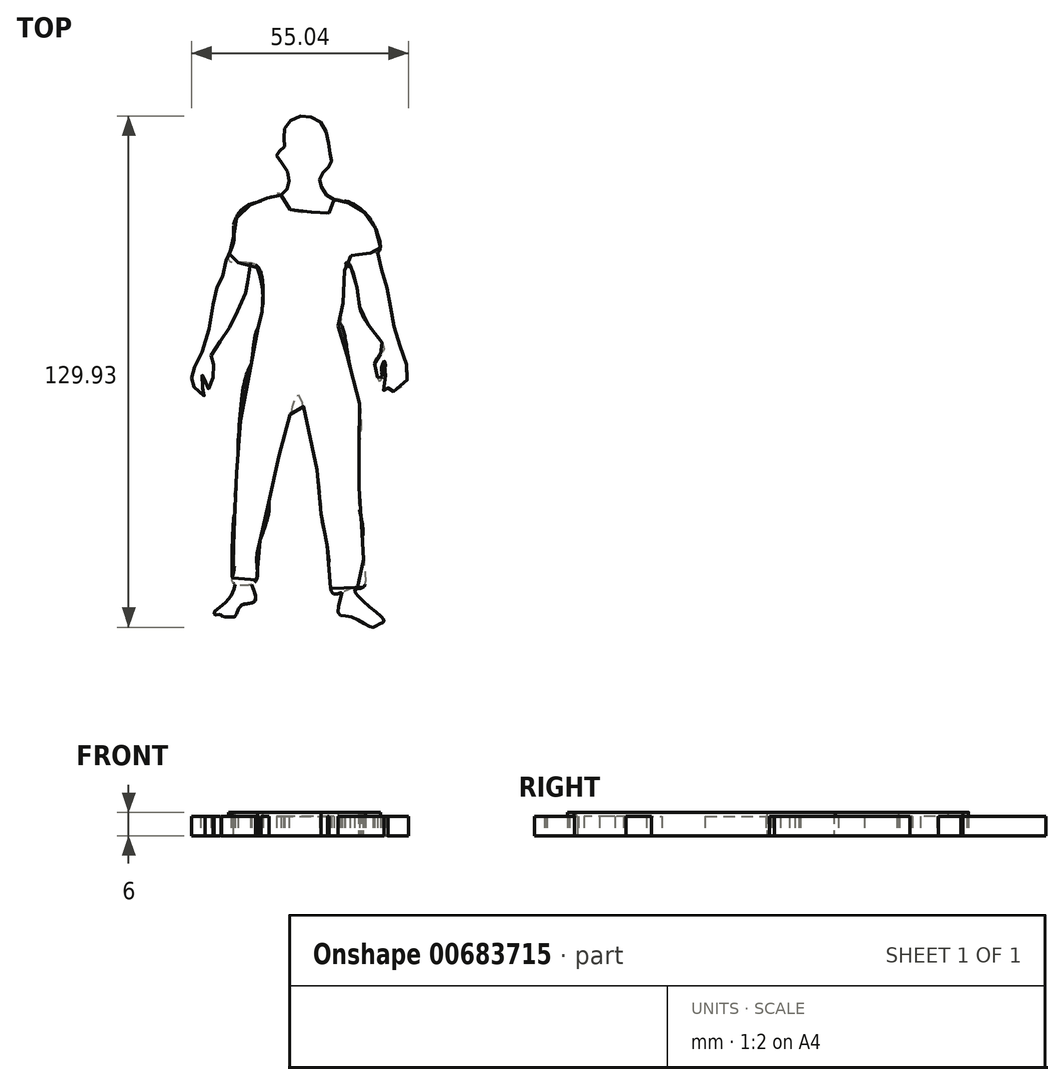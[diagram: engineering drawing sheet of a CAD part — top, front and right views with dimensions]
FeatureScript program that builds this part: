
annotation { "Feature Type Name" : "Feature", "Feature Type Description" : "" }
export const myFeature = defineFeature(function(context is Context, id is Id, definition is map)
    precondition{}
    {
        {
            var Q0;
            Q0=qCreatedBy(makeId("Top.planeOp"),FACE);
            var sketch = newSketch(context, id + "F0", { "sketchPlane" : qUnion([Q0])});
            skFitSpline(sketch, "E0", {"points": [v(-30.35, 51.78) * mm, v(-29.82, 47) * mm, v(-33, 44.36) * mm, v(-40.42, 42.24) * mm, v(-43.6, 37.47) * mm, v(-43.6, 33.23) * mm, v(-44.13, 31.38) * mm, v(-45.45, 29) * mm, v(-46.5, 23.96) * mm, v(-47.83, 21.58) * mm, v(-49.42, 13.37) * mm, v(-52.6, 3.03) * mm, v(-54.2, 0) * mm, v(-54.2, -2.26) * mm, v(-53.66, -3.85) * mm, v(-51.01, -5.97) * mm, v(-51.01, -4.91) * mm, v(-52.07, -2.26) * mm, v(-51.01, 0) * mm, v(-51.01, -3.85) * mm, v(-49.42, -3.85) * mm, v(-48.9, 0) * mm, v(-48.9, 2.5) * mm, v(-49.42, 4.1) * mm, v(-46.24, 8.86) * mm, v(-43.6, 13.63) * mm, v(-40.42, 20.52) * mm, v(-40.15, 22.1) * mm, v(-39.1, 28.2) * mm, v(-37.24, 25.29) * mm, v(-36.18, 18.93) * mm, v(-36.97, 11.51) * mm, v(-38.03, 9.13) * mm, v(-38.03, 5.68) * mm, v(-40.15, 0) * mm, v(-41.48, -5.97) * mm, v(-42.54, -19.22) * mm, v(-42.54, -25.05) * mm, v(-43.6, -36.44) * mm, v(-43.6, -53.66) * mm, v(-43.33, -53.66) * mm, v(-44.65, -57.37) * mm, v(-48.63, -61.07) * mm, v(-48.36, -61.6) * mm, v(-47.57, -61.6) * mm, v(-46.77, -61.6) * mm, v(-46.77, -61.87) * mm, v(-45.45, -62.13) * mm, v(-44.13, -62.13) * mm, v(-43.33, -62.13) * mm, v(-42, -59.49) * mm, v(-39.36, -58.7) * mm, v(-38.03, -57.37) * mm, v(-39.1, -53.66) * mm, v(-38.83, -53.66) * mm, v(-38.3, -47.83) * mm, v(-34.85, -36.44) * mm, v(-34.59, -29.82) * mm, v(-31.94, -18.69) * mm, v(-27.17, -4.91) * mm, v(-22.93, -20.28) * mm, v(-20.28, -31.93) * mm, v(-20.28, -37.23) * mm, v(-17.1, -55.78) * mm, v(-16.04, -55.51) * mm, v(-17.1, -61.07) * mm, v(-13.93, -62.13) * mm, v(-8.63, -64.78) * mm, v(-7.04, -64.25) * mm, v(-5.45, -63.2) * mm, v(-8.63, -60.02) * mm, v(-12.87, -55.25) * mm, v(-10.75, -54.72) * mm, v(-11.28, -52.07) * mm, v(-10.75, -41.47) * mm, v(-11.8, -34.58) * mm, v(-12.87, -26.64) * mm, v(-11.8, -17.1) * mm, v(-11.8, -10.74) * mm, v(-14.46, 3.56) * mm, v(-16.04, 11.51) * mm, v(-16.84, 13.1) * mm, v(-16.04, 23.96) * mm, v(-14.72, 27.94) * mm, v(-12.34, 21.58) * mm, v(-10.48, 13.63) * mm, v(-5.45, 5.95) * mm, v(-7.57, 3.56) * mm, v(-7.3, 0) * mm, v(-6.5, -2.26) * mm, v(-5.45, 0) * mm, v(-5.98, 0) * mm, v(-5.45, 2.77) * mm, v(-5.18, -2.26) * mm, v(-5.45, -4.65) * mm, v(-4.39, -3.85) * mm, v(-4.39, -4.91) * mm, v(0, -2.8) * mm, v(0, 2.77) * mm, v(-2.8, 11.51) * mm, v(-4.39, 19.99) * mm, v(-6.5, 27.94) * mm, v(-7.57, 34.3) * mm, v(-8.63, 38.53) * mm, v(-14.46, 43.3) * mm, v(-18.16, 43.83) * mm, v(-21.34, 47) * mm, v(-21.34, 50.19) * mm, v(-18.96, 52.84) * mm, v(-19.22, 56.02) * mm, v(-21.08, 62.9) * mm, v(-26.64, 65.02) * mm, v(-30.88, 61.31) * mm, v(-30.88, 57.08) * mm, v(-32.73, 55.49) * mm, v(-30.35, 51.78) * mm]});
            skSolve(sketch);
        }
        {
            var Q0;
            Q0=qCreatedBy(makeId("Top.planeOp"),FACE);
            var sketch = newSketch(context, id + "F1", { "sketchPlane" : qUnion([Q0])});
            skFitSpline(sketch, "E1", {"points": [v(-37.24, 11.51) * mm, v(-31.67, 11.51) * mm, v(-16.57, 11.51) * mm, v(-15.78, 9.13) * mm, v(-13.66, 0) * mm, v(-11.28, -11.27) * mm, v(-11.8, -20.28) * mm, v(-11.8, -27.96) * mm, v(-11.8, -34.05) * mm, v(-10.75, -41.47) * mm, v(-10.75, -46.24) * mm, v(-10.48, -54.45) * mm, v(-12.87, -54.72) * mm, v(-18.16, -56.3) * mm, v(-19.22, -51) * mm, v(-20.28, -42) * mm, v(-21.34, -37.76) * mm, v(-21.34, -32.46) * mm, v(-24, -17.1) * mm, v(-27.44, -5.7) * mm, v(-29.82, -13.4) * mm, v(-31.94, -20.8) * mm, v(-34.59, -32.2) * mm, v(-35.65, -38.82) * mm, v(-37.77, -47.3) * mm, v(-38.3, -53.4) * mm, v(-43.6, -53.66) * mm, v(-43.6, -50.48) * mm, v(-43.6, -37.23) * mm, v(-42.54, -21.34) * mm, v(-41.48, -8.89) * mm, v(-39.1, 2.5) * mm, v(-37.24, 11.51) * mm]});
            skSolve(sketch);
        }
        {
            var Q0;
            Q0=qCreatedBy(makeId("Top.planeOp"),FACE);
            var sketch = newSketch(context, id + "F2", { "sketchPlane" : qUnion([Q0])});
            skFitSpline(sketch, "E2", {"points": [v(-31.94, 45.42) * mm, v(-29.82, 41.71) * mm, v(-23.46, 40.65) * mm, v(-19.22, 40.65) * mm, v(-18.16, 43.83) * mm, v(-14.98, 43.3) * mm, v(-10.75, 40.92) * mm, v(-7.3, 35.88) * mm, v(-6.5, 31.11) * mm, v(-8.36, 30.32) * mm, v(-13.93, 29.52) * mm, v(-15.51, 25.29) * mm, v(-16.84, 12.04) * mm, v(-18.7, 11.51) * mm, v(-28.76, 11.25) * mm, v(-37.24, 10.98) * mm, v(-36.7, 14.16) * mm, v(-36.18, 19.99) * mm, v(-38.3, 27.4) * mm, v(-44.65, 28.2) * mm, v(-43.6, 33.23) * mm, v(-43.6, 37.47) * mm, v(-40.42, 41.98) * mm, v(-35.91, 43.83) * mm, v(-31.94, 45.42) * mm]});
            skSolve(sketch);
        }
        {
            var Q0;
            Q0 = qSketchRegion(id + "F0", true);
            extrude(context, id + "F3", {"entities" : qUnion([Q0]), "depth" : 5 * mm, "offsetDistance" : 25.4 * mm});
        }
        {
            var Q0;
            Q0 = qSketchRegion(id + "F1", true);
            extrude(context, id + "F4", {"entities" : qUnion([Q0]), "operationType" : NewBodyOperationType.ADD, "depth" : 6 * mm, "offsetDistance" : 25.4 * mm});
        }
        {
            var Q0;
            Q0 = qSketchRegion(id + "F2", true);
            extrude(context, id + "F5", {"entities" : qUnion([Q0]), "operationType" : NewBodyOperationType.ADD, "depth" : 6 * mm, "offsetDistance" : 25.4 * mm});
        }
    });
